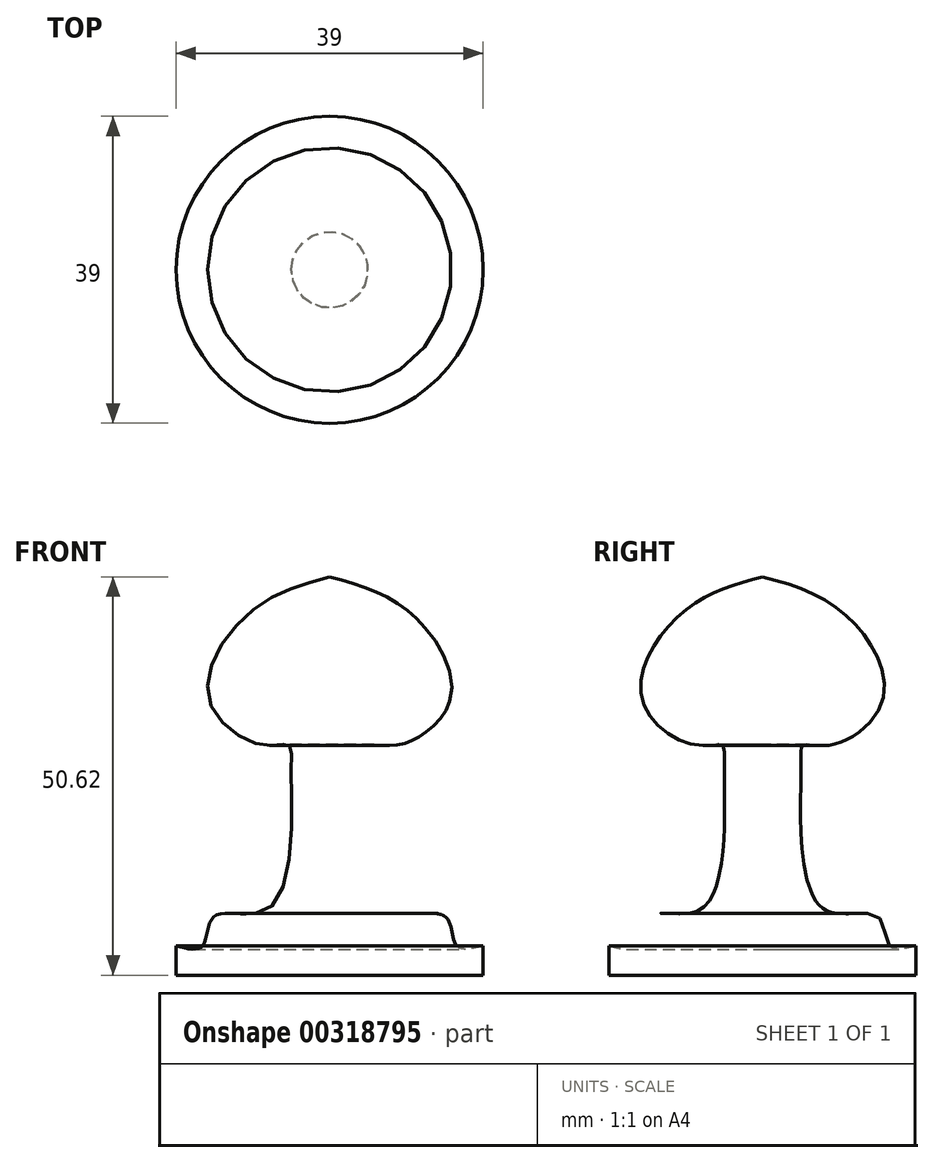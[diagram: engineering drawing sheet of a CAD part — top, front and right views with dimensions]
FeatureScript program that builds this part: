
annotation { "Feature Type Name" : "Feature", "Feature Type Description" : "" }
export const myFeature = defineFeature(function(context is Context, id is Id, definition is map)
    precondition{}
    {
        {
            var Q0;
            Q0=qCreatedBy(makeId("Front.planeOp"),FACE);
            var sketch = newSketch(context, id + "F0", { "sketchPlane" : qUnion([Q0])});
            skLineSegment(sketch, "E0", {"start": v(0, -76.31) * mm, "end": v(-19.5, -76.31) * mm});
            skLineSegment(sketch, "E1", {"start": v(-19.5, -76.31) * mm, "end": v(-19.5, -72.56) * mm});
            skFitSpline(sketch, "E2", {"points": [v(-19.5, -72.56) * mm, v(-16.13, -72.56) * mm, v(-14.63, -68.81) * mm, v(-7.5, -67.69) * mm, v(-4.88, -49.69) * mm, v(-5.25, -47.06) * mm, v(-8.63, -47.06) * mm, v(-15.38, -41.06) * mm, v(-10.13, -30.19) * mm, v(0, -25.69) * mm], "startDerivative": vector(54.11, -14.83) * mm, "endDerivative": vector(76.05, 20.52) * mm});
            skLineSegment(sketch, "E3", {"start": v(0, -25.69) * mm, "end": v(0, -76.31) * mm});
            skSolve(sketch);
        }
        {
            var Q0;
            Q0=qCreatedBy(makeId("Front.planeOp"),FACE);
            var sketch = newSketch(context, id + "F1", { "sketchPlane" : qUnion([Q0])});
            skLineSegment(sketch, "E4", {"start": v(0, 47.06) * mm, "end": v(0, -95.82) * mm, "construction": true});
            skSolve(sketch);
        }
        {
            var Q0;
            Q0=makeQuery(id+"F0.imprint","IMPRINT",FACE,{"disambiguationData":[TD([[makeQuery(id+"F0.imprint","IMPRINT",EDGE,{"derivedFrom":sQuery(id+"F0.wireOp",EDGE,"E0")}),-1.0]])]});
            var Q1;
            Q1=sQuery(id+"F1.wireOp",EDGE,"E4");
            revolve(context, id + "F2", {"entities" : qUnion([Q0]), "axis" : qUnion([Q1]), "revolveType" : RevolveType.FULL});
        }
    });
